# Revit family: ASSA_ABLOY_FT100
name_source: partatom
category: Generic Models
units: mm (PartAtom-declared; Revit-internal decimal feet)

## family parameters
Always vertical = Yes
Can host rebar = No
Cut with Voids When Loaded = No
Part Type = Normal
Room Calculation Point = No
Round Connector Dimension = Use Diameter
Shared = No
Work Plane-Based = No

## types (1)
- FT100
    Access control/Biometrics = Yes
    AccessoryOptions = Contact manufacturer
    Anti-tailgating/Anti-piggybacking = Yes
    AntiFingerTrapRequirement = No
    BreakoutFacility = No
    Burglar resistance = No
    Colour = Customer specific
    Construction Type = Full-height turnstile
    Default Elevation = 0 mm  [stored 0 ft]
    Description = Full height turnstile
    DoorIncluded = Yes
    DoorsetFasteners = Screws
    DoorsetOperation = Automatic
    DoorsetOptions = no
    DrumWallOptions = Metal
    ElectronicLock = Yes
    FireExit = No
    FrameFinishOptions = Powder coated, Anodized, Clad in stainless steel, etc.
    FrameProfile = Aluminium
    FrameSeal = Yes
    GlassLayers = 0
    GlassThickness1 = 0 mm  [stored 0 ft]
    GlassThickness2 = 0 mm  [stored 0 ft]
    HandicapAccessible = No
    HasDrive = Yes
    HeightUnderCanopyOptions = 2125
    IsExternal = Yes
    LeafColourOptions = All RAL, customer specific
    Manufacturer = Tansa
    ManufacturerURL = https://www.assaabloyentrance.com
    Material = Aluminum
    Model = Maxima
    ModelReference = Depends on the configuration
    NominalHeight = 2370 mm  [stored 7.77559 ft]
    NominalLength = 1220 mm  [stored 4.00262 ft]
    NominalWidth = 1441 mm  [stored 4.72769 ft]
    OperatingTemperature = -20º to +70ºC
    PassageWidthOptions = 600, 630, 670
    ReplacementCost = Depends on the configuration and door type
    SafetyDevices = Force Limitations
    SelfClosing = Yes
    ServiceLifeDuration = 10-15 years
    Shape = Cylinder shaped
    ThresholdRequired = No
    URL = https://www.assaabloyentrance.com
    WarrantyDescription = Depends on country
    Weight = Depends on configuration and size

note: [stored X ft] marks values corroborated as IEEE doubles in the binary element streams (Revit-internal decimal feet)

## geometry (parser evidence)
native form markers: Sweep x16
no freeform markers — native parametric forms only
